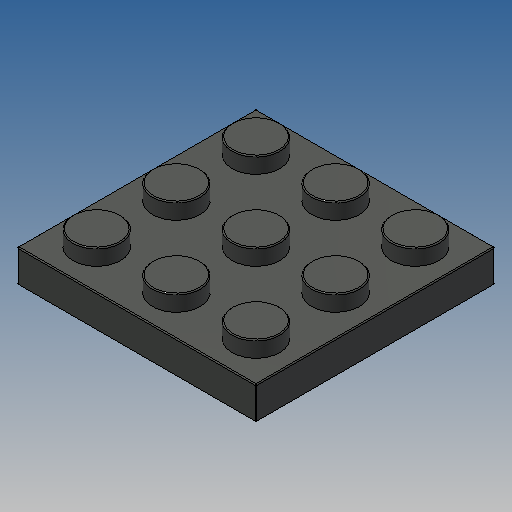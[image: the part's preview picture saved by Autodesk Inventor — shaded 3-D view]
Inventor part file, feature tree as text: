
AUTODESK INVENTOR PART (.ipt)
format: ipt  version: 2025 (Build 290162010, 162A)  size: 220,672 bytes
history: native  units: in
note: dims shown in document units (in); Inventor stores cm internally (conversion verified against a paired STEP export)
features: extrude x4, sketch x3, fillet x2, pattern_linear x2
ambient origin geometry x8: Origin, YZ Plane, XZ Plane, XY Plane, X Axis, Y Axis, Z Axis, Center Point
bodies: Solid1 (feature_tree)
feature tree (11):
  extrude  "Extrusion1"  Depth=0.9449in
  extrude  "Extrusion4"  Depth=0.063in
  fillet  "Fillet2"  Radius=0.063in
  pattern_linear  "Rectangular Pattern1"  Spacing1=0.2564in  [1 undecoded]
  sketch  "Sketch3"  dims[d4=0.126in d5=0.0in d7=0.0591in d8=0.063in d11=0.063in d12=0.0in]
  extrude  "Extrusion2"  Depth=0.189in
  extrude  "Extrusion5"  Depth=0.063in
  pattern_linear  "Rectangular Pattern2"  Spacing1=0.189in  [1 undecoded]
  fillet  "Fillet1"  Radius=0.1575in
  sketch  "Sketch2"  dims[d0=0.9449in d1=0.9449in]
  sketch  "Sketch9"  dims[d22=0.0039in d60=0.2564in d61=0.189in d62=0.063in d63=0.189in d64=0.1575in d65=0.1575in d66=0.063in d67=0.0in d68=0.0039in d69=1.1811in d71=0.315in d72=1.1811in d74=0.315in d75=0.315in d76=0.315in d77=0.0709in d78=0.0in d79=0.7874in d81=0.315in d82=0.7874in d84=0.315in d85=0.0in d86=0.0in d87=0.0in d88=0.0in d89=0.0in d90=0.0in d91=0.0in]
note: 2 required parameter values undecoded (feature->parameter linkage not recoverable at this tier; creation-order binding heuristic only, values carry confidence <= 0.55)
